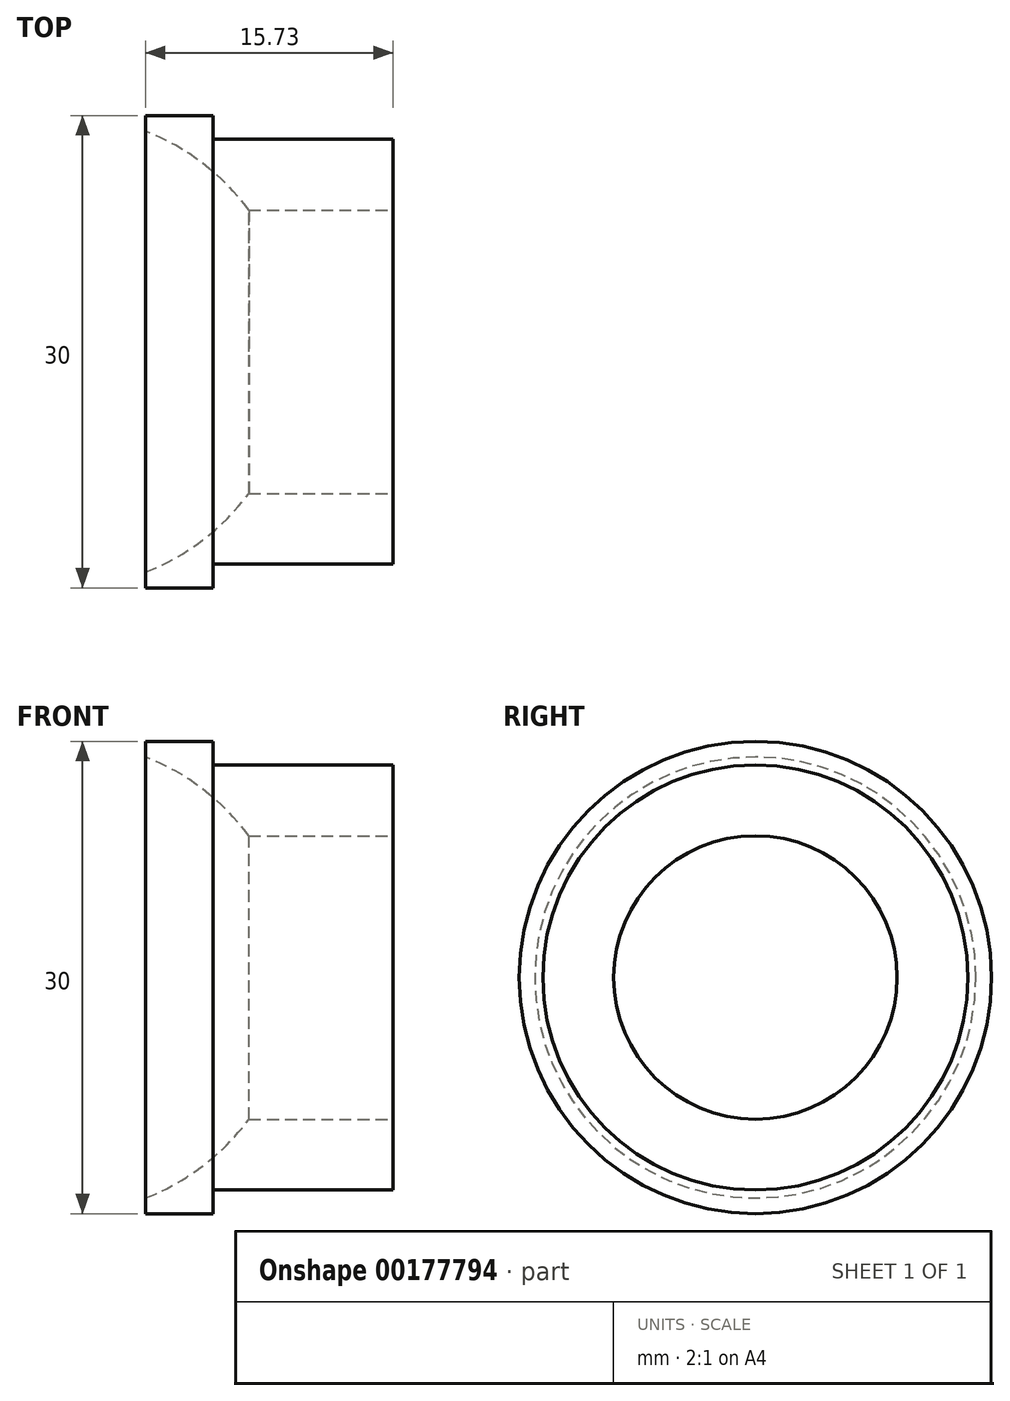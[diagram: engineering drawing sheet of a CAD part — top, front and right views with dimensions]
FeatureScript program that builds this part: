
annotation { "Feature Type Name" : "Feature", "Feature Type Description" : "" }
export const myFeature = defineFeature(function(context is Context, id is Id, definition is map)
    precondition{}
    {
        {
            var Q0;
            Q0=qCreatedBy(makeId("Front.planeOp"),FACE);
            var sketch = newSketch(context, id + "F0", { "sketchPlane" : qUnion([Q0])});
            skLineSegment(sketch, "E0", {"start": v(0, 0) * mm, "end": v(-30.33, 0) * mm, "construction": true});
            skLineSegment(sketch, "E1", {"start": v(21.23, 13.5) * mm, "end": v(21.23, 9) * mm});
            skLineSegment(sketch, "E2", {"start": v(21.23, 9) * mm, "end": v(12.06, 9) * mm});
            skArc(sketch, "E3", {"start": v(1.23, 15) * mm, "mid": v(-3.4, -14.66) * mm, "end": v(5.5, 14) * mm, "construction": true});
            skLineSegment(sketch, "E4", {"start": v(21.23, 13.5) * mm, "end": v(9.8, 13.5) * mm});
            skLineSegment(sketch, "E5", {"start": v(9.8, 15) * mm, "end": v(5.5, 15) * mm});
            skArc(sketch, "E6", {"start": v(12.06, 9) * mm, "mid": v(9.13, 11.96) * mm, "end": v(5.5, 14) * mm});
            skLineSegment(sketch, "E7", {"start": v(9.8, 15) * mm, "end": v(9.8, 13.5) * mm});
            skLineSegment(sketch, "E8", {"start": v(5.5, 15) * mm, "end": v(5.5, 14) * mm});
            skSolve(sketch);
        }
        {
            var Q0;
            Q0 = qSketchRegion(id + "F0", true);
            var Q1;
            Q1=sQuery(id+"F0.wireOp",EDGE,"E0");
            revolve(context, id + "F1", {"entities" : qUnion([Q0]), "axis" : qUnion([Q1]), "revolveType" : RevolveType.FULL});
        }
    });
